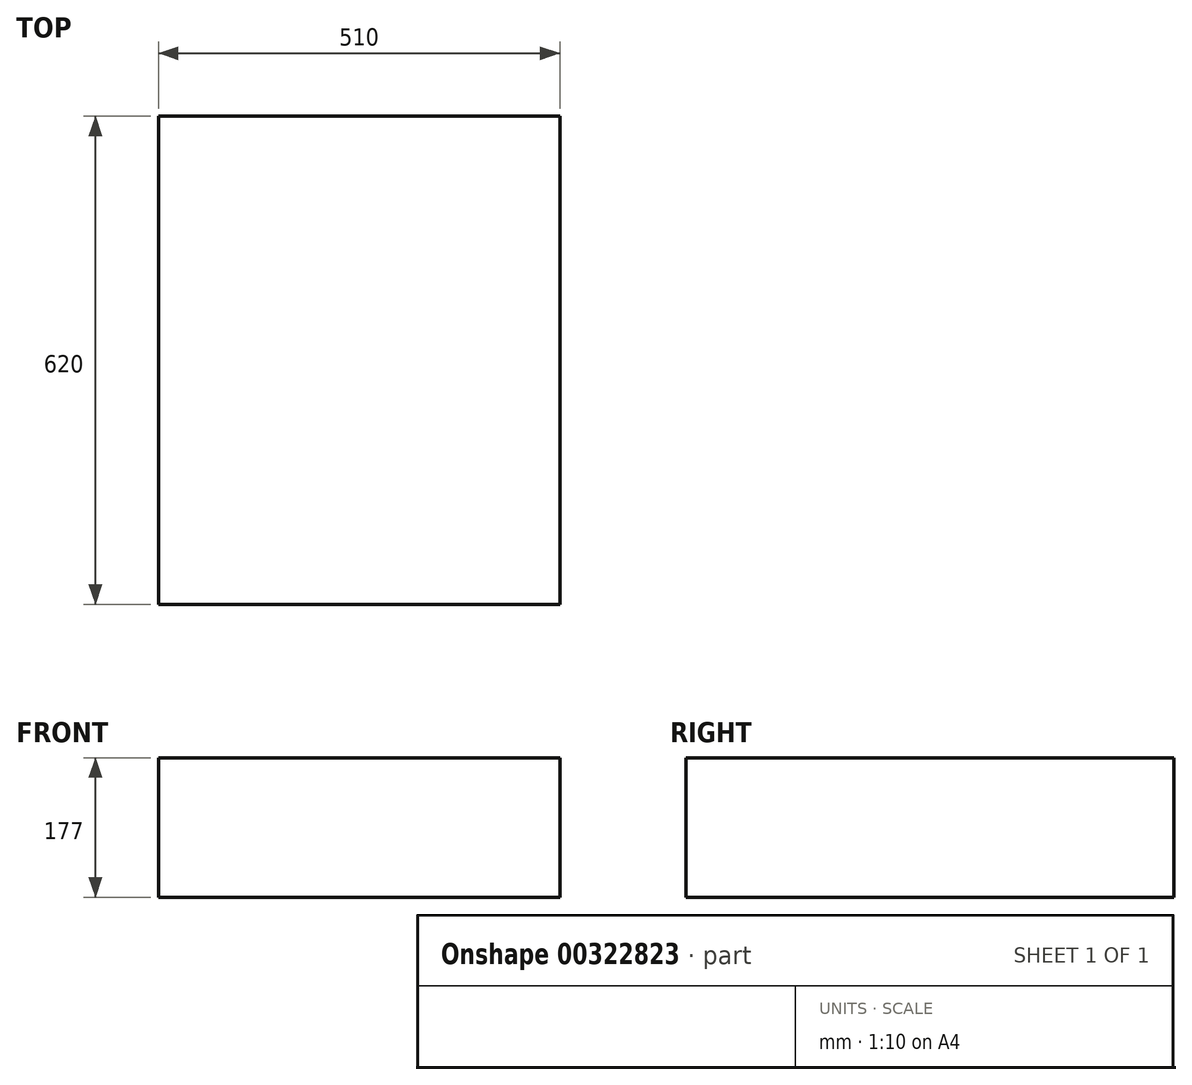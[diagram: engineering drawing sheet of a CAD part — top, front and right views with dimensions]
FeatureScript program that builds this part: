
annotation { "Feature Type Name" : "Feature", "Feature Type Description" : "" }
export const myFeature = defineFeature(function(context is Context, id is Id, definition is map)
    precondition{}
    {
        {
            var Q0;
            Q0=qCreatedBy(makeId("Top.planeOp"),FACE);
            var sketch = newSketch(context, id + "F0", { "sketchPlane" : qUnion([Q0])});
            skLineSegment(sketch, "E0.bottom", {"start": v(255, -310) * mm, "end": v(-255, -310) * mm});
            skLineSegment(sketch, "E0.top", {"start": v(255, 310) * mm, "end": v(-255, 310) * mm});
            skLineSegment(sketch, "E0.left", {"start": v(255, -310) * mm, "end": v(255, 310) * mm});
            skLineSegment(sketch, "E0.right", {"start": v(-255, -310) * mm, "end": v(-255, 310) * mm});
            skPoint(sketch, "E0.middle", {"position": v(0, 0) * mm});
            skSolve(sketch);
        }
        {
            var Q0;
            Q0=makeQuery(id+"F0.imprint","IMPRINT",FACE,{"disambiguationData":[TD([[makeQuery(id+"F0.imprint","IMPRINT",EDGE,{"derivedFrom":sQuery(id+"F0.wireOp",EDGE,"E0.bottom")}),-1.0]])]});
            extrude(context, id + "F1", {"entities" : qUnion([Q0]), "oppositeDirection" : true, "depth" : 177 * mm});
        }
    });
